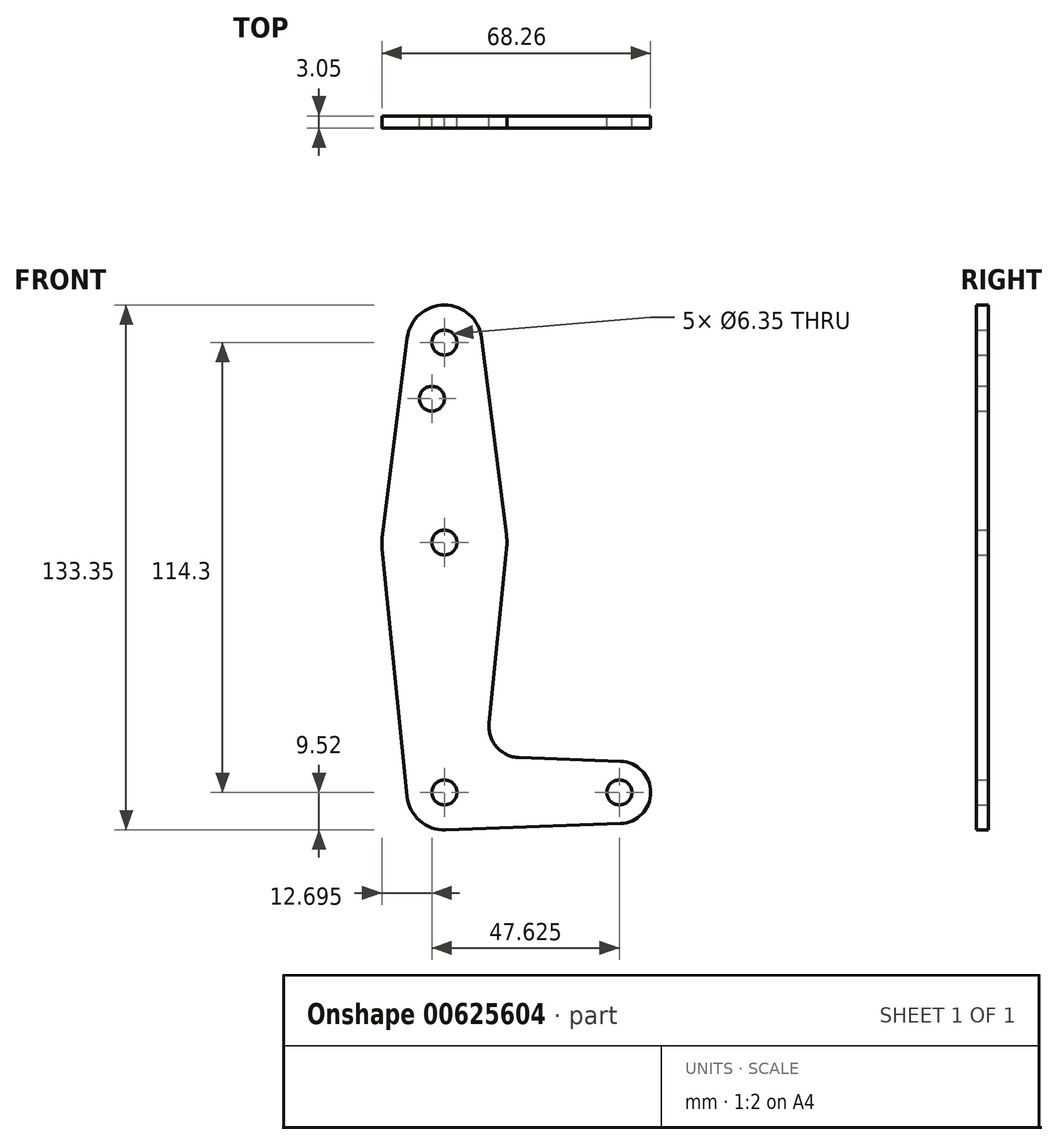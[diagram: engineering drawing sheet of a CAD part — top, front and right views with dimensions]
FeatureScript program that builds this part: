
annotation { "Feature Type Name" : "Feature", "Feature Type Description" : "" }
export const myFeature = defineFeature(function(context is Context, id is Id, definition is map)
    precondition{}
    {
        {
            var Q0;
            Q0=qCreatedBy(makeId("Front.planeOp"),FACE);
            var sketch = newSketch(context, id + "F0", { "sketchPlane" : qUnion([Q0])});
            skLineSegment(sketch, "E0", {"start": v(0, 114.3) * mm, "end": v(0, 0) * mm, "construction": true});
            skLineSegment(sketch, "E1", {"start": v(0, 0) * mm, "end": v(44.45, 0) * mm, "construction": true});
            skCircle(sketch, "E2", {"center": v(0, 114.3) * mm, "radius": 9.52 * mm});
            skCircle(sketch, "E3", {"center": v(0, 63.5) * mm, "radius": 15.88 * mm});
            skCircle(sketch, "E4", {"center": v(0, 0) * mm, "radius": 9.52 * mm});
            skCircle(sketch, "E5", {"center": v(44.45, 0) * mm, "radius": 7.94 * mm});
            skLineSegment(sketch, "E6", {"start": v(-9.45, 115.5) * mm, "end": v(-15.75, 65.48) * mm});
            skLineSegment(sketch, "E7", {"start": v(15.8, 61.91) * mm, "end": v(11.34, 17.6) * mm});
            skLineSegment(sketch, "E8", {"start": v(-15.8, 61.91) * mm, "end": v(-9.48, -0.95) * mm});
            skLineSegment(sketch, "E9", {"start": v(9.45, 115.5) * mm, "end": v(15.75, 65.48) * mm});
            skLineSegment(sketch, "E10", {"start": v(18.97, 8.85) * mm, "end": v(44.73, 7.93) * mm});
            skLineSegment(sketch, "E11", {"start": v(0.34, -9.52) * mm, "end": v(44.73, -7.93) * mm});
            skCircle(sketch, "E12", {"center": v(0, 114.3) * mm, "radius": 3.18 * mm});
            skCircle(sketch, "E13", {"center": v(0, 63.5) * mm, "radius": 3.18 * mm});
            skCircle(sketch, "E14", {"center": v(0, 0) * mm, "radius": 3.18 * mm});
            skCircle(sketch, "E15", {"center": v(44.45, 0) * mm, "radius": 3.18 * mm});
            skCircle(sketch, "E16", {"center": v(-3.18, 100.03) * mm, "radius": 3.18 * mm});
            skArc(sketch, "E17.filletArc", {"start": v(11.34, 17.6) * mm, "mid": v(13.26, 11.57) * mm, "end": v(18.97, 8.85) * mm});
            skSolve(sketch);
        }
        {
            var Q0;
            Q0 = qSketchRegion(id + "F0", true);
            extrude(context, id + "F1", {"entities" : qUnion([Q0]), "depth" : 3.05 * mm, "offsetDistance" : 25.4 * mm});
        }
    });
